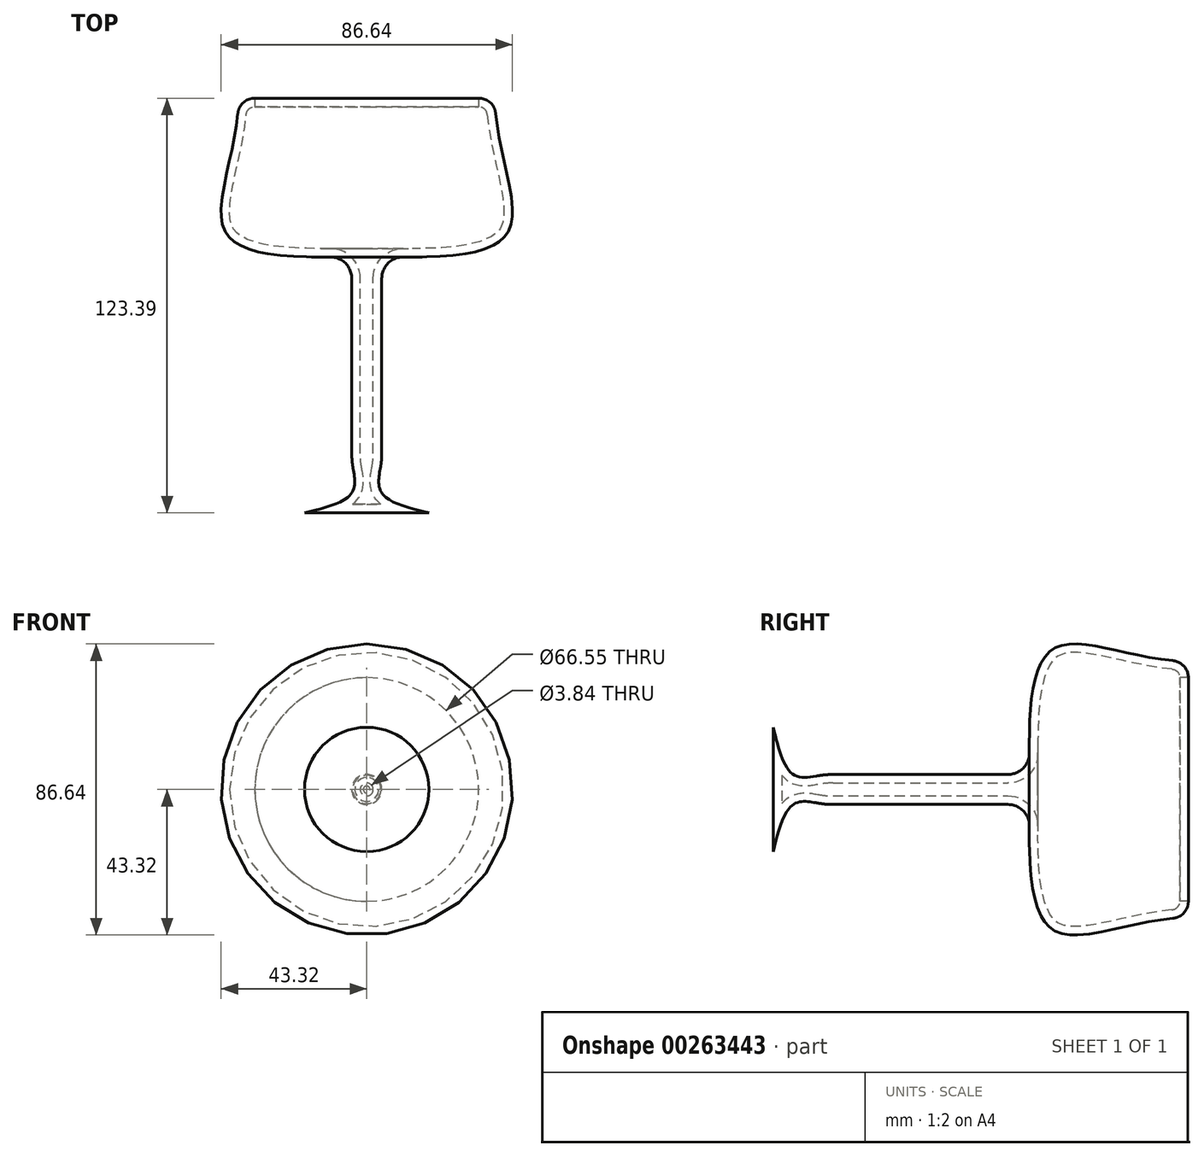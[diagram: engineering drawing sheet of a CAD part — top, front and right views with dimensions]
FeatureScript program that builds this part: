
annotation { "Feature Type Name" : "Feature", "Feature Type Description" : "" }
export const myFeature = defineFeature(function(context is Context, id is Id, definition is map)
    precondition{}
    {
        {
            var Q0;
            Q0=qCreatedBy(makeId("Top.planeOp"),FACE);
            var sketch = newSketch(context, id + "F0", { "sketchPlane" : qUnion([Q0])});
            skLineSegment(sketch, "E0", {"start": v(-4.46, -58.52) * mm, "end": v(-4.46, -6.45) * mm});
            skPoint(sketch, "E1.visualSharp", {"position": v(-4.46, -64.22) * mm});
            skFitSpline(sketch, "E2", {"points": [v(-4.46, 0) * mm, v(-41.77, 6.92) * mm, v(-38.1, 47.16) * mm], "startDerivative": vector(-91.03, -1.79) * mm, "endDerivative": vector(0.47, 95.48) * mm});
            skLineSegment(sketch, "E3", {"start": v(-38.1, 47.16) * mm, "end": v(0, 47.16) * mm});
            skLineSegment(sketch, "E4", {"start": v(0, 47.16) * mm, "end": v(0, -76.23) * mm});
            skArc(sketch, "E5.filletArc", {"start": v(-4.46, -6.45) * mm, "mid": v(-6.34, -1.94) * mm, "end": v(-10.88, -0.1) * mm});
            skFitSpline(sketch, "E6", {"points": [v(-4.46, -61.3) * mm, v(-4.46, -70.3) * mm, v(-18.5, -76.23) * mm], "startDerivative": vector(5.39, -22.91) * mm, "endDerivative": vector(-31.83, -7.62) * mm});
            skLineSegment(sketch, "E7", {"start": v(-18.5, -76.23) * mm, "end": v(0, -76.23) * mm});
            skArc(sketch, "E8.filletArc", {"start": v(-4.46, -58.52) * mm, "mid": v(-4.34, -61.04) * mm, "end": v(-3.96, -63.55) * mm});
            skSolve(sketch);
        }
        {
            var Q0;
            Q0 = qSketchRegion(id + "F0", true);
            var Q1;
            Q1=sQuery(id+"F0.wireOp",EDGE,"E4");
            revolve(context, id + "F1", {"entities" : qUnion([Q0]), "axis" : qUnion([Q1]), "revolveType" : RevolveType.FULL});
        }
        {
            var Q0;
            Q0=makeQuery(id+"F1.opRevolve","SWEPT_FACE",FACE,{"disambiguationData":[OSD([sQuery(id+"F0.wireOp",EDGE,"E2")])]});
            fillet(context, id + "F2", {"entities" : qUnion([Q0]), "radius" : 5.08 * mm, "tangentPropagation" : true, "allowEdgeOverflow" : false});
        }
        {
            var Q0;
            Q0=makeQuery(id+"F1.opRevolve","SWEPT_FACE",FACE,{"disambiguationData":[OSD([sQuery(id+"F0.wireOp",EDGE,"E3")])]});
            shell(context, id + "F3", {"entities" : qUnion([Q0]), "thickness" : 2.54 * mm});
        }
    });
